# Revit family: Haworth_Planes_ConferenceDesk_EU_PRELIMINARY
name_source: partatom
category: Furniture
units: mm (PartAtom-declared; Revit-internal decimal feet)

## family parameters
Always vertical = Yes
Cut with Voids When Loaded = No
OmniClass Number = 23.40.70.14.64.21
OmniClass Title = Systems Furniture
Room Calculation Point = No
Shared = No
Work Plane-Based = No

## types (7) — shared parameters
Actual Height = 74 cm
Assembly Code = E2020200
Caster Finish = Haworth _ Polymer _ Black
Description = Haworth - Planes - Conference Table
Edge Protector = Haworth _ Polymer _ Black
Flip Top Finish = Haworth _ Paint _ Undecided _ Table
Leg Height = 72 cm
Manufacturer = Haworth
Max. Depth = 80 cm
Max. Width = 210 cm
Min. Depth = 65 cm
Min. Width = 100 cm
Model = A00000012
Revision Number = 1
Size = Verify Final Dim. w/ Haworth
Trim Finish = Haworth _ Polymer _ Undecided
URL = https://www.haworth.com
URL - Product = https://www.haworth.com
Warranty = http://www.haworth.com

## per-type parameters (varying)
| type | Actual Depth | Actual Width | Angled Single Leg | Casters | Depth | Flip Top | Glides | Rounded Corners | Screen Width | Squared Corners | Straight Legs | Table Linking | Width | With Screen |
| 100w x 70d | 70 cm | 100 cm | No | Yes | 70 cm | No | No | Yes | 50 cm | No | Yes | No | 100 cm | No |
| 120w x 65d | 65 cm | 120 cm | Yes | No | 65 cm | Yes | Yes | No | 70 cm | Yes | No | Yes | 120 cm | Yes |
| 140w x 75d | 75 cm | 140 cm | No | Yes | 75 cm | No | No | Yes | 90 cm | No | Yes | No | 140 cm | No |
| 150w x 70d | 70 cm | 150 cm | Yes | No | 70 cm | Yes | Yes | No | 100 cm | Yes | No | Yes | 150 cm | Yes |
| 160w x 80d | 80 cm | 160 cm | No | Yes | 80 cm | No | No | Yes | 110 cm | No | Yes | No | 160 cm | No |
| 180w x 80d | 80 cm | 180 cm | Yes | No | 80 cm | Yes | Yes | No | 130 cm | Yes | No | Yes | 180 cm | Yes |
| 210w x 80d | 80 cm | 210 cm | Yes | Yes | 80 cm | Yes | No | Yes | 160 cm | No | No | Yes | 210 cm | Yes |

## geometry (parser evidence)
native form markers: Sweep x29
no freeform markers — native parametric forms only
